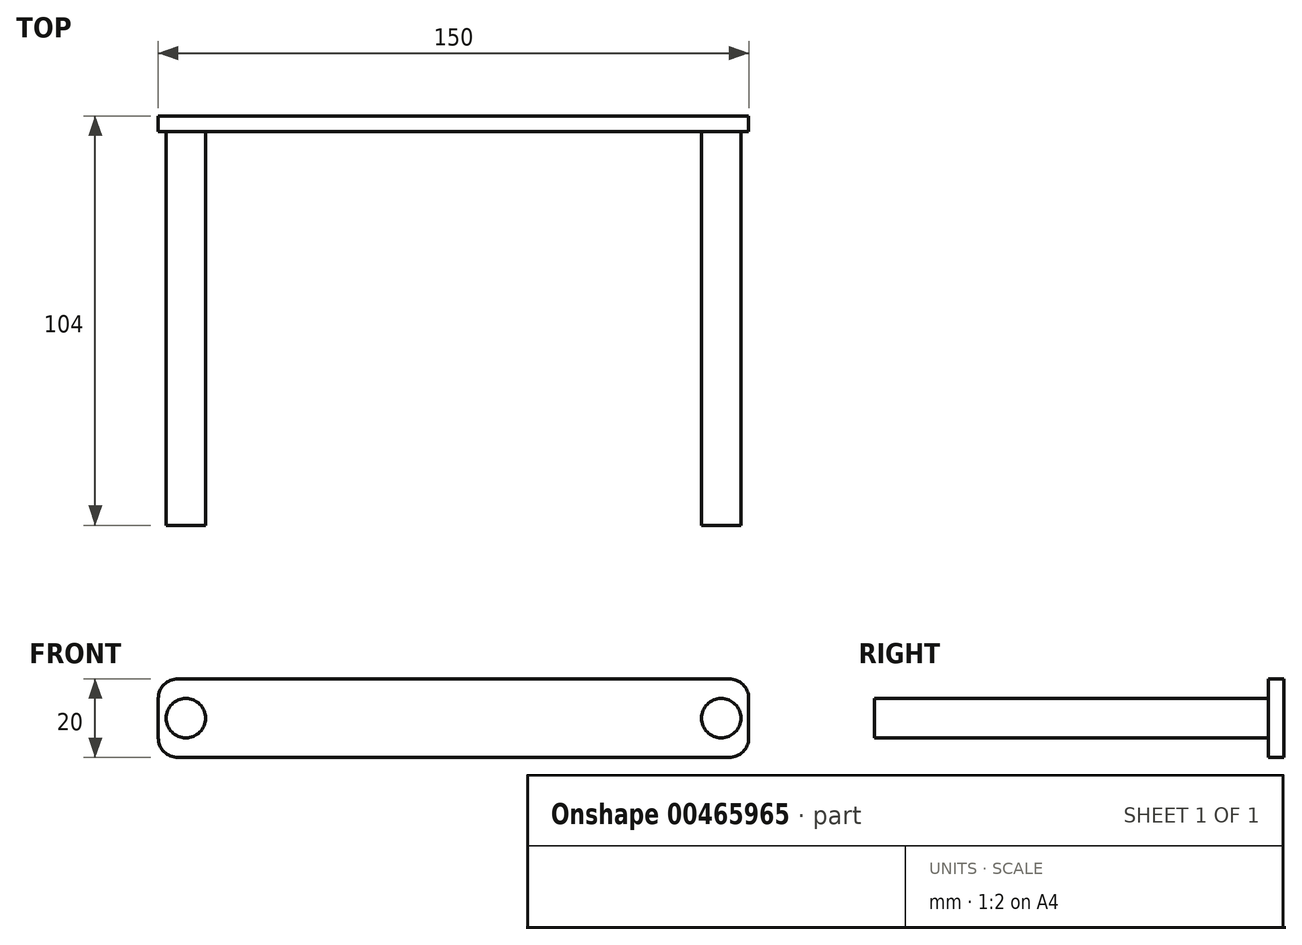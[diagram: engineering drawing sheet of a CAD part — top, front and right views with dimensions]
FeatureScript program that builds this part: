
annotation { "Feature Type Name" : "Feature", "Feature Type Description" : "" }
export const myFeature = defineFeature(function(context is Context, id is Id, definition is map)
    precondition{}
    {
        {
            var Q0;
            Q0=qCreatedBy(makeId("Front.planeOp"),FACE);
            var sketch = newSketch(context, id + "F0", { "sketchPlane" : qUnion([Q0])});
            skLineSegment(sketch, "E0.bottom", {"start": v(-74.67, -47.73) * mm, "end": v(75.33, -47.73) * mm});
            skLineSegment(sketch, "E0.top", {"start": v(-74.67, -67.73) * mm, "end": v(75.33, -67.73) * mm});
            skLineSegment(sketch, "E0.left", {"start": v(-74.67, -47.73) * mm, "end": v(-74.67, -67.73) * mm});
            skLineSegment(sketch, "E0.right", {"start": v(75.33, -47.73) * mm, "end": v(75.33, -67.73) * mm});
            skSolve(sketch);
        }
        {
            var Q0;
            Q0 = qSketchRegion(id + "F0", true);
            extrude(context, id + "F1", {"entities" : qUnion([Q0]), "depth" : 4 * mm});
        }
        {
            var Q0;
            Q0=makeQuery(id+"F1.opExtrude","CAP_FACE",FACE,{"disambiguationData":[OSD([sQuery(id+"F0.wireOp",EDGE,"E0.bottom"),sQuery(id+"F0.wireOp",EDGE,"E0.top"),sQuery(id+"F0.wireOp",EDGE,"E0.left"),sQuery(id+"F0.wireOp",EDGE,"E0.right")])],"isStart":false});
            var sketch = newSketch(context, id + "F2", { "sketchPlane" : qUnion([Q0])});
            skCircle(sketch, "E1", {"center": v(68.33, -57.73) * mm, "radius": 5 * mm});
            skCircle(sketch, "E2", {"center": v(-67.67, -57.73) * mm, "radius": 5 * mm});
            skSolve(sketch);
        }
        {
            var Q0;
            Q0 = qSketchRegion(id + "F2", true);
            extrude(context, id + "F3", {"entities" : qUnion([Q0]), "operationType" : NewBodyOperationType.ADD, "depth" : 100 * mm});
        }
        {
            var Q0;
            Q0=makeQuery(id+"F1.opExtrude","SWEPT_EDGE",EDGE,{"disambiguationData":[OSD([sQuery(id+"F0.wireOp",EDGE,"E0.top"),sQuery(id+"F0.wireOp",EDGE,"E0.left")])]});
            var Q1;
            Q1=makeQuery(id+"F1.opExtrude","SWEPT_EDGE",EDGE,{"disambiguationData":[OSD([sQuery(id+"F0.wireOp",EDGE,"E0.bottom"),sQuery(id+"F0.wireOp",EDGE,"E0.left")])]});
            var Q2;
            Q2=makeQuery(id+"F1.opExtrude","SWEPT_EDGE",EDGE,{"disambiguationData":[OSD([sQuery(id+"F0.wireOp",EDGE,"E0.top"),sQuery(id+"F0.wireOp",EDGE,"E0.right")])]});
            var Q3;
            Q3=makeQuery(id+"F1.opExtrude","SWEPT_EDGE",EDGE,{"disambiguationData":[OSD([sQuery(id+"F0.wireOp",EDGE,"E0.bottom"),sQuery(id+"F0.wireOp",EDGE,"E0.right")])]});
            fillet(context, id + "F4", {"entities" : qUnion([Q0, Q1, Q2, Q3]), "radius" : 5 * mm, "tangentPropagation" : true, "allowEdgeOverflow" : false});
        }
    });
